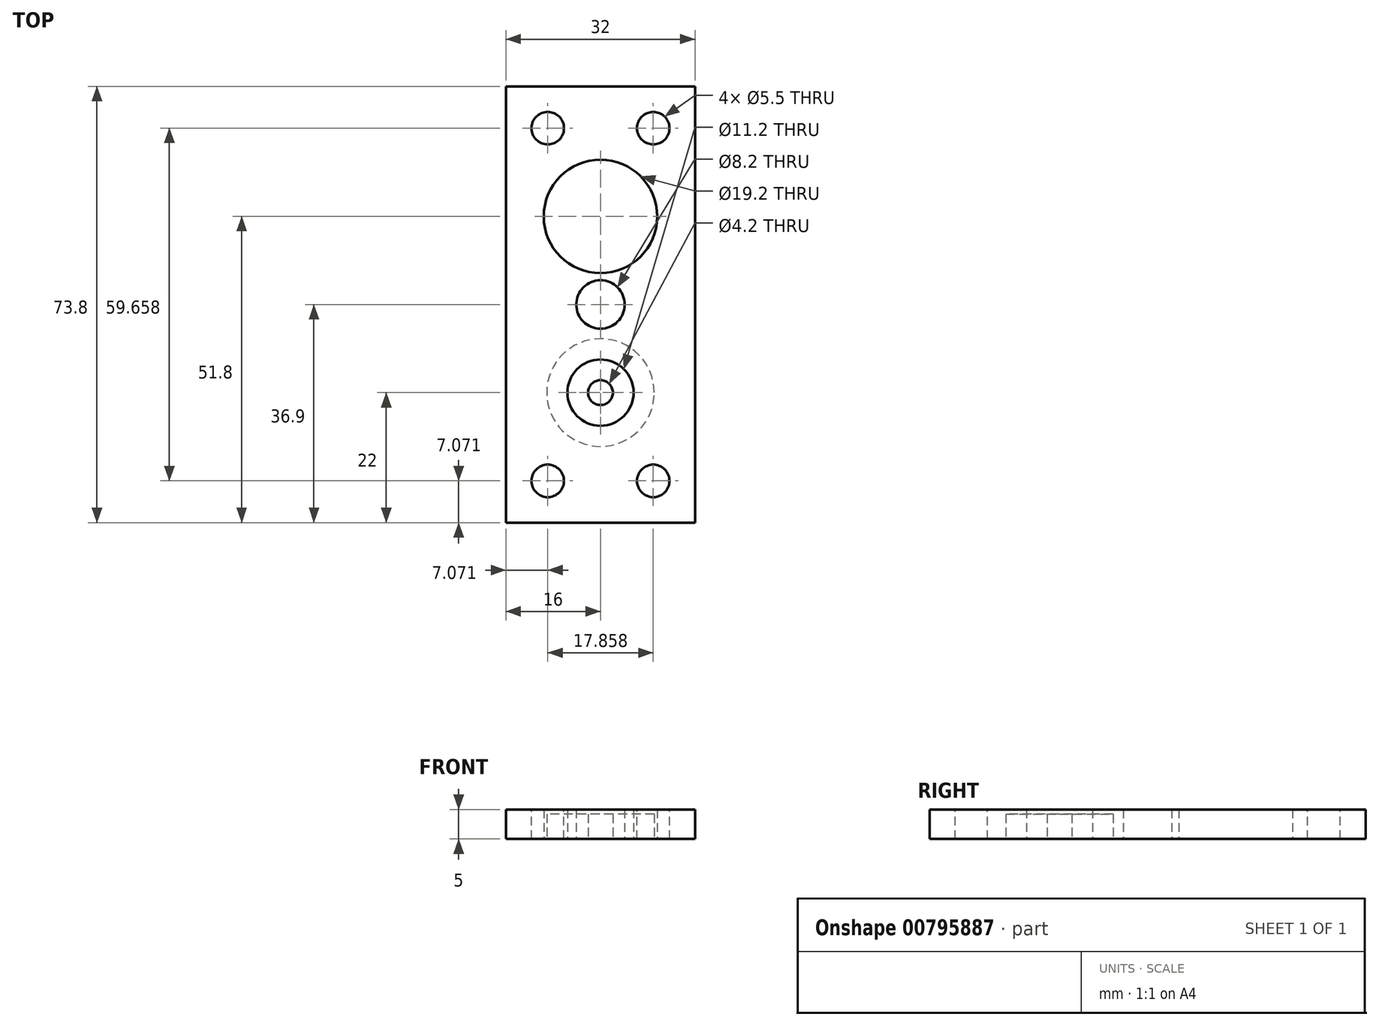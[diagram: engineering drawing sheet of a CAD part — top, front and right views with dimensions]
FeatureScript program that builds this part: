
annotation { "Feature Type Name" : "Feature", "Feature Type Description" : "" }
export const myFeature = defineFeature(function(context is Context, id is Id, definition is map)
    precondition{}
    {
        {
            assignVariable(context, id + "F0", {"name" : "Thickness", "anyValue" : 5 * mm});
        }
        {
            var Q0;
            Q0=qCreatedBy(makeId("Top.planeOp"),FACE);
            var sketch = newSketch(context, id + "F1", { "sketchPlane" : qUnion([Q0])});
            skCircle(sketch, "E0", {"center": v(0, 0) * mm, "radius": 5.6 * mm});
            skCircle(sketch, "E1", {"center": v(0, 14.9) * mm, "radius": 4.1 * mm});
            skCircle(sketch, "E2", {"center": v(0, 29.8) * mm, "radius": 9.6 * mm});
            skLineSegment(sketch, "E3.bottom", {"start": v(-16, 51.8) * mm, "end": v(16, 51.8) * mm});
            skLineSegment(sketch, "E3.top", {"start": v(-16, -22) * mm, "end": v(16, -22) * mm});
            skLineSegment(sketch, "E3.left", {"start": v(-16, 51.8) * mm, "end": v(-16, -22) * mm});
            skLineSegment(sketch, "E3.right", {"start": v(16, 51.8) * mm, "end": v(16, -22) * mm});
            skLineSegment(sketch, "E4", {"start": v(-16, 29.8) * mm, "end": v(16, 29.8) * mm, "construction": true});
            skLineSegment(sketch, "E5", {"start": v(0, 0) * mm, "end": v(0, -22) * mm, "construction": true});
            skCircle(sketch, "E6", {"center": v(0, 29.8) * mm, "radius": 14.4 * mm, "construction": true});
            skCircle(sketch, "E7", {"center": v(0, 0) * mm, "radius": 14.4 * mm, "construction": true});
            skCircle(sketch, "E8", {"center": v(0, 14.9) * mm, "radius": 5.9 * mm, "construction": true});
            skCircle(sketch, "E9", {"center": v(0, 29.8) * mm, "radius": 8 * mm, "construction": true});
            skCircle(sketch, "E10", {"center": v(0, 0) * mm, "radius": 8 * mm, "construction": true});
            skSolve(sketch);
        }
        {
            var Q0;
            Q0=makeQuery(id+"F1.imprint","IMPRINT",FACE,{"disambiguationData":[TD([[makeQuery(id+"F1.imprint","IMPRINT",EDGE,{"derivedFrom":sQuery(id+"F1.wireOp",EDGE,"E0")}),-1.0]])]});
            extrude(context, id + "F2", {"entities" : qUnion([Q0]), "depth" : getVariable(context, 'Thickness'), "offsetDistance" : 25 * mm});
        }
        {
            var Q0;
            Q0=makeQuery(id+"F2.opExtrude","CAP_FACE",FACE,{"disambiguationData":[OSD([sQuery(id+"F1.wireOp",EDGE,"E0"),sQuery(id+"F1.wireOp",EDGE,"E1"),sQuery(id+"F1.wireOp",EDGE,"E2"),sQuery(id+"F1.wireOp",EDGE,"E3.bottom"),sQuery(id+"F1.wireOp",EDGE,"E3.top"),sQuery(id+"F1.wireOp",EDGE,"E3.left"),sQuery(id+"F1.wireOp",EDGE,"E3.right")])],"isStart":false});
            var sketch = newSketch(context, id + "F3", { "sketchPlane" : qUnion([Q0])});
            skPoint(sketch, "E11.0", {"position": v(-16, 51.8) * mm});
            skPoint(sketch, "E12.0", {"position": v(16, 51.8) * mm});
            skPoint(sketch, "E13.0", {"position": v(16, -22) * mm});
            skPoint(sketch, "E14.0", {"position": v(-16, -22) * mm});
            skLineSegment(sketch, "E15", {"start": v(0, 51.8) * mm, "end": v(0, 48.36) * mm, "construction": true});
            skLineSegment(sketch, "E16", {"start": v(-16, 51.8) * mm, "end": v(-8.93, 44.73) * mm, "construction": true});
            skLineSegment(sketch, "E17", {"start": v(-16, 14.9) * mm, "end": v(-10.5, 14.9) * mm, "construction": true});
            skLineSegment(sketch, "E18.MirrorCS", {"start": v(16, 51.8) * mm, "end": v(8.93, 44.73) * mm, "construction": true});
            skLineSegment(sketch, "E19.MirrorCS", {"start": v(-16, -22) * mm, "end": v(-8.93, -14.93) * mm, "construction": true});
            skLineSegment(sketch, "E20.MirrorCS", {"start": v(16, -22) * mm, "end": v(8.93, -14.93) * mm, "construction": true});
            skSolve(sketch);
        }
        {
            var Q0;
            Q0=sQuery(id+"F3.wireOp",VERTEX,"E16.end");
            var Q1;
            Q1=sQuery(id+"F3.wireOp",VERTEX,"E18.MirrorCS.end");
            var Q2;
            Q2=sQuery(id+"F3.wireOp",VERTEX,"E20.MirrorCS.end");
            var Q3;
            Q3=sQuery(id+"F3.wireOp",VERTEX,"E19.MirrorCS.end");
            var Q4;
            Q4=makeQuery(id+"F2.opExtrude","SWEPT_BODY",BODY,{"disambiguationData":[OSD([sQuery(id+"F1.wireOp",EDGE,"E0"),sQuery(id+"F1.wireOp",EDGE,"E1"),sQuery(id+"F1.wireOp",EDGE,"E2"),sQuery(id+"F1.wireOp",EDGE,"E3.bottom"),sQuery(id+"F1.wireOp",EDGE,"E3.top"),sQuery(id+"F1.wireOp",EDGE,"E3.left"),sQuery(id+"F1.wireOp",EDGE,"E3.right")])]});
            hole(context, id + "F4", {"style" : HoleStyle.SIMPLE, "endStyle" : HoleEndStyle.BLIND, "standardTappedOrClearance" : lookupTablePath({ "standard" : "ISO", "fit" : "Normal", "size" : "M5", "type" : "Clearance" }), "standardBlindInLast" : lookupTablePath({ "fit" : "Standard", "standard" : "ISO", "size" : "M5", "type" : "Clearance" }), "holeDiameter" : 5.5 * mm, "majorDiameter" : 5 * mm, "holeDepth" : 14.4 * mm, "isTappedThrough" : true, "tappedDepth" : 12 * mm, "tapClearance" : 3, "locations" : qUnion([Q0, Q1, Q2, Q3]), "scope" : qUnion([Q4])});
        }
        {
            var Q0;
            Q0=qCreatedBy(makeId("Top.planeOp"),FACE);
            var sketch = newSketch(context, id + "F5", { "sketchPlane" : qUnion([Q0])});
            skCircle(sketch, "E21", {"center": v(0, 0) * mm, "radius": 2.1 * mm});
            skCircle(sketch, "E22.0", {"center": v(0, 0) * mm, "radius": 9.1 * mm});
            skSolve(sketch);
        }
        {
            var Q0;
            Q0 = qSketchRegion(id + "F5", true);
            extrude(context, id + "F6", {"entities" : qUnion([Q0]), "depth" : 4.2 * mm, "offsetDistance" : 25 * mm});
        }
    });
